# Revit family: Genie_Site_ArticulatingBoom_Z34a
name_source: partatom
category: Site
revit_build: Autodesk Revit 2017 (Build: 20160225_1515(x64)
units: mm (PartAtom-declared; Revit-internal decimal feet)

## family parameters
Always vertical = Yes
Cut with Voids When Loaded = No
OmniClass Number = 23.50.85.17.11
OmniClass Title = Electric and Battery Telescoping Platforms
Part Type = Normal
Round Connector Dimension = Use Diameter
Shared = No
Work Plane-Based = No

## types (1)
- Z34 - 22N
    Assembly Code = E1030900
    AssetType = Fixed
    BIMObjectName = Genie_Site_ArticulatingBoom_Z34
    ClassificationName = Uniclass2015
    ClassificationValue = Pr_65_80_47_95
    Color = Grey & Blue
    Cost = 0 $
    Description = The Genie® Z®-34/22 N electric articulating boom lift offers quiet, emission-free operation in the most sensitive work environments, as a 48V DC machine.
    DocumentationLiterature = https://www.genielift.com
    DocumentationTechnical = https://www.genielift.com
    DurationUnit = Years
    ExpectedLife = 0
    Features = 30% gradeability drive performance and 4.0 mph travel speed, Motor controller eliminates the need for forward/reverse contactors or speed sensors, reducing complexity and improving reliability of the drive system, Self-leveling platform features 180° powered horizontal rotation for precise positioning and easy operation, Versatile 40 ft 6 in (12.52 m) working height, 22 ft 3 in (6.78 m) horizontal reach.
    Finish = Painted Steel
    IfcExportAs = IfcTransportElement
    IfcExportType = IfcTransportElementType
    Keynote = X
    Manufacturer = Genie
    ManufacturerName = Genie
    Material = Painted Steel
    Model = Genie - Articulating Boom
    ModelNumber = Z34 - 22N
    ModelReference = Genie - Articulating Boom
    NBSDescription = Vertical lifting platforms
    NBSObjectName = Genie - Vertical lifting platforms
    NBSReference = 90-80-65/350
    NominalDepth = 1420 mm
    NominalHeight = 2000 mm  [stored 6.56168 ft]
    NominalLength = 5720 mm
    ProductionYear = 2018
    ReplacementCost = 0
    Size = 1.47m x 2m x 5.72m
    Type Comments = Z34 - 22N
    TypeName = Genie - Articulating Boom
    URL = http://www.genielift.co.uk
    WarrantyDurationLabor = 0
    WarrantyDurationParts = 0
    WarrantyDurationUnit = Years
    WarrantyGuarantorLabor = http://www.genielift.co.uk
    WarrantyGuarantorParts = http://www.genielift.co.uk
    _BSBibleVersion = 15
    _BimSpecGuid = 0
    _CurrentRevision = 1
    _DistributedBy = www.bimstore.co.uk

note: [stored X ft] marks values corroborated as IEEE doubles in the binary element streams (Revit-internal decimal feet)

## geometry (parser evidence)
native form markers: Sweep x50
no freeform markers — native parametric forms only
